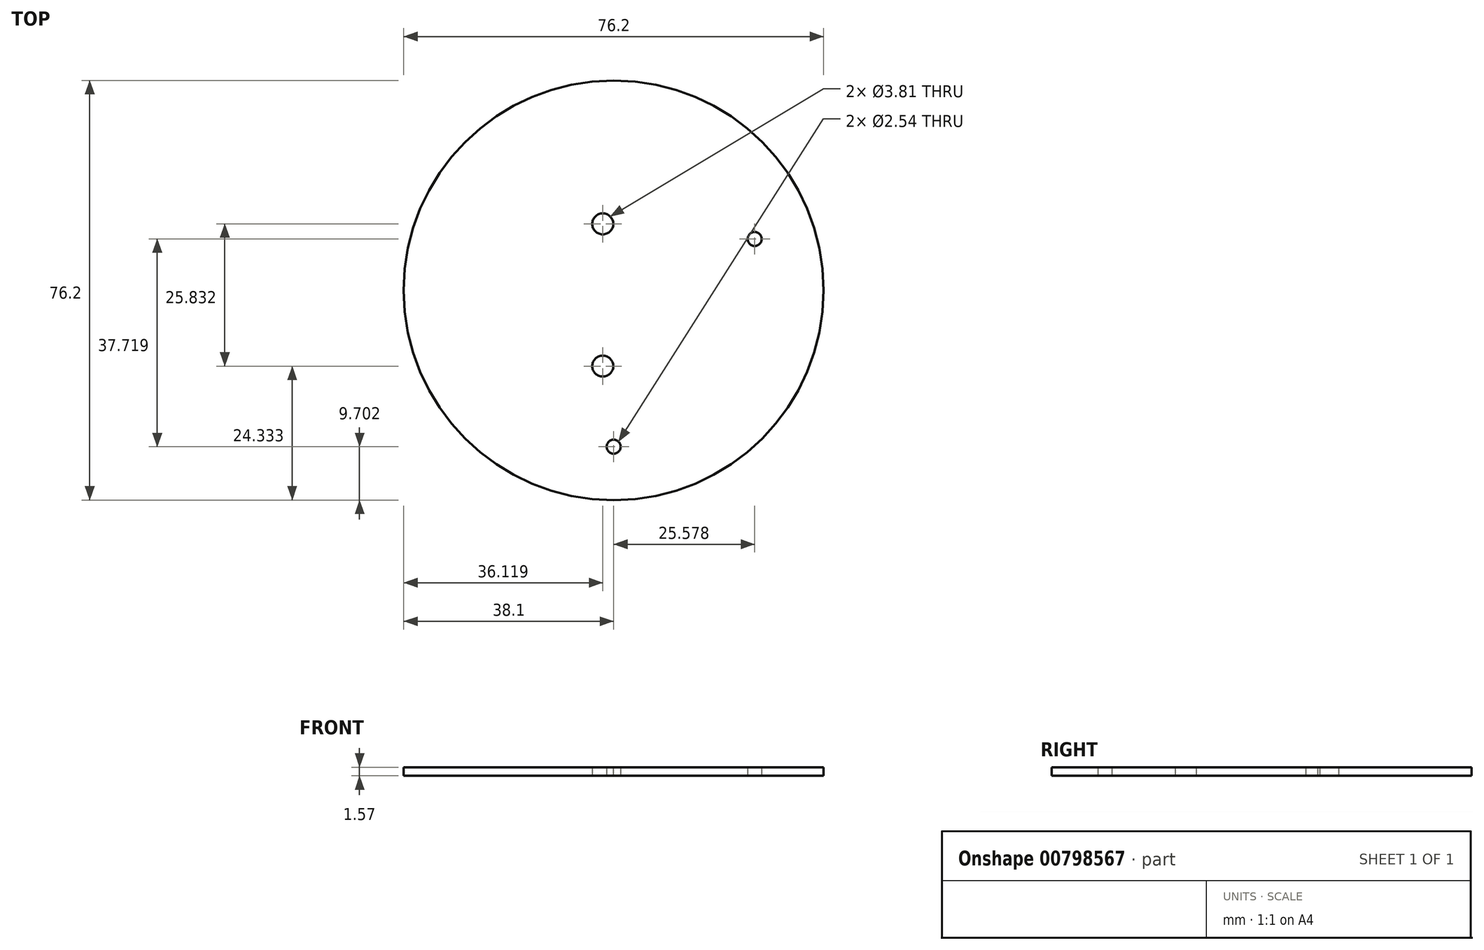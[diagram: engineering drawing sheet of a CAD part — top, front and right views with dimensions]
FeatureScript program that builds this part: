
annotation { "Feature Type Name" : "Feature", "Feature Type Description" : "" }
export const myFeature = defineFeature(function(context is Context, id is Id, definition is map)
    precondition{}
    {
        {
            var Q0;
            Q0=qCreatedBy(makeId("Top.planeOp"),FACE);
            var sketch = newSketch(context, id + "F0", { "sketchPlane" : qUnion([Q0])});
            skCircle(sketch, "E0", {"center": v(0, 0) * mm, "radius": 38.1 * mm});
            skCircle(sketch, "E1.1.0", {"center": v(-1.98, 12.07) * mm, "radius": 1.9 * mm});
            skCircle(sketch, "E1.2.0", {"center": v(-1.98, -13.77) * mm, "radius": 1.9 * mm});
            skCircle(sketch, "E1.3.0", {"center": v(25.58, 9.32) * mm, "radius": 1.27 * mm});
            skCircle(sketch, "E2", {"center": v(0, -28.4) * mm, "radius": 1.27 * mm});
            skSolve(sketch);
        }
        {
            var Q0;
            Q0 = qSketchRegion(id + "F0", true);
            extrude(context, id + "F1", {"entities" : qUnion([Q0]), "depth" : 1.57 * mm, "offsetDistance" : 25.4 * mm});
        }
    });
